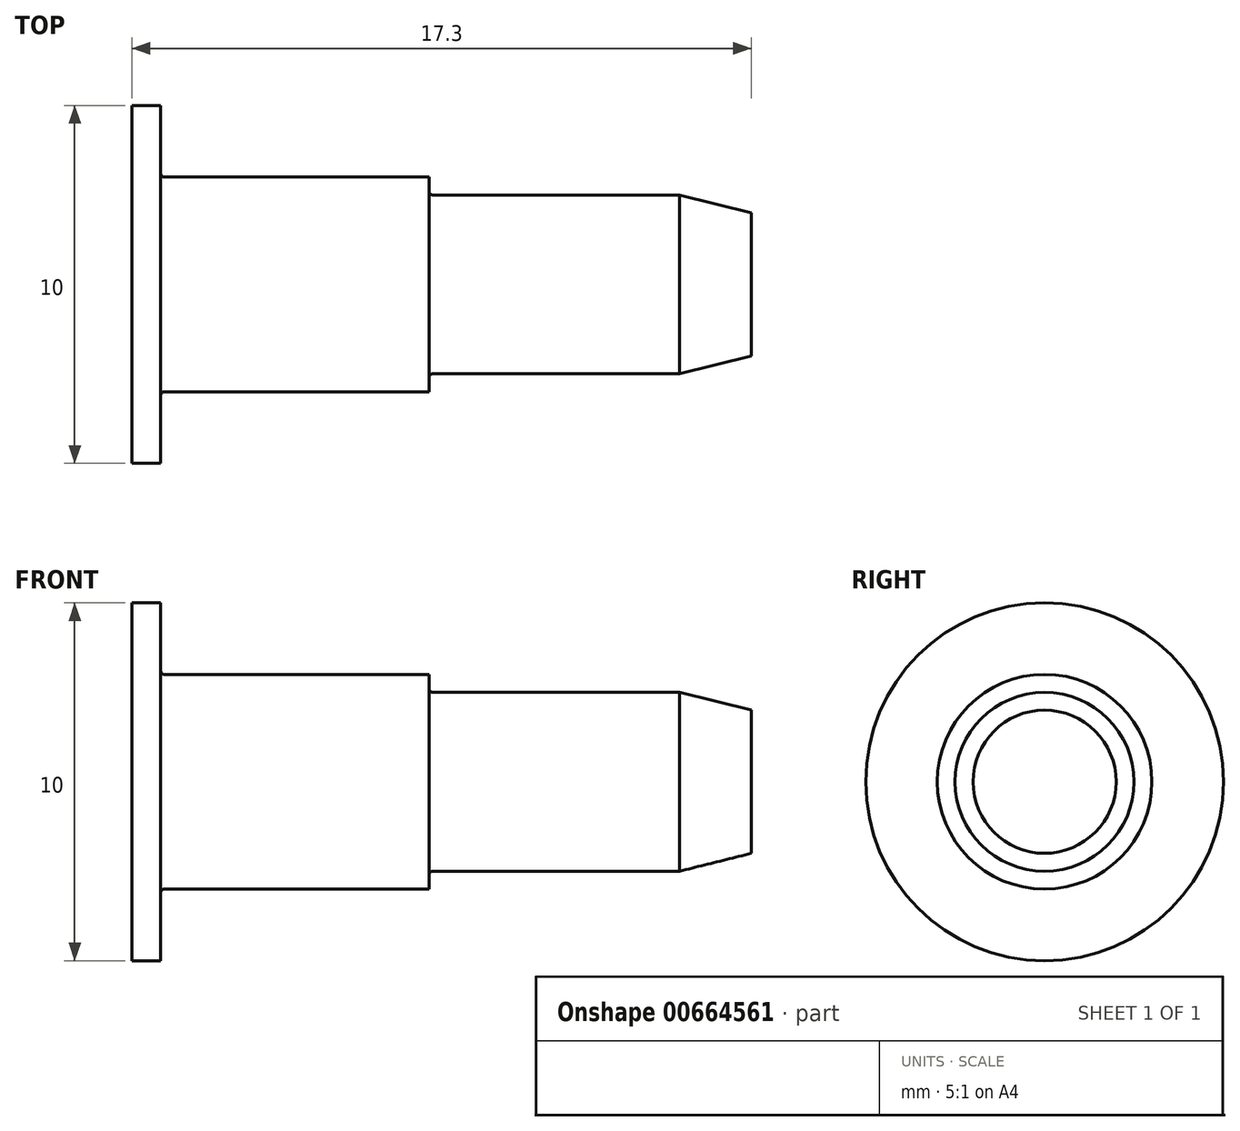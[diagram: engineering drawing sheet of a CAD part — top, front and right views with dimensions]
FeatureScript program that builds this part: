
annotation { "Feature Type Name" : "Feature", "Feature Type Description" : "" }
export const myFeature = defineFeature(function(context is Context, id is Id, definition is map)
    precondition{}
    {
        {
            var Q0;
            Q0=qCreatedBy(makeId("Front.planeOp"),FACE);
            var sketch = newSketch(context, id + "F0", { "sketchPlane" : qUnion([Q0])});
            skLineSegment(sketch, "E0", {"start": v(0, 0) * mm, "end": v(0, 5) * mm});
            skLineSegment(sketch, "E1", {"start": v(0, 5) * mm, "end": v(0.8, 5) * mm});
            skLineSegment(sketch, "E2", {"start": v(0.8, 5) * mm, "end": v(0.8, 3.1) * mm});
            skArc(sketch, "E3", {"start": v(0.8, 3.1) * mm, "mid": v(0.83, 3.03) * mm, "end": v(0.9, 3) * mm});
            skLineSegment(sketch, "E4", {"start": v(0.9, 3) * mm, "end": v(8.3, 3) * mm});
            skLineSegment(sketch, "E5", {"start": v(8.3, 3) * mm, "end": v(8.3, 2.6) * mm});
            skLineSegment(sketch, "E6", {"start": v(17.3, 2) * mm, "end": v(17.3, 0) * mm});
            skLineSegment(sketch, "E7", {"start": v(17.3, 0) * mm, "end": v(0, 0) * mm});
            skLineSegment(sketch, "E8", {"start": v(8.4, 2.5) * mm, "end": v(15.3, 2.5) * mm});
            skLineSegment(sketch, "E9", {"start": v(15.3, 2.5) * mm, "end": v(17.3, 2) * mm});
            skArc(sketch, "E10", {"start": v(8.3, 2.6) * mm, "mid": v(8.33, 2.53) * mm, "end": v(8.4, 2.5) * mm});
            skSolve(sketch);
        }
        {
            var Q0;
            Q0=makeQuery(id+"F0.imprint","IMPRINT",FACE,{"disambiguationData":[TD([[makeQuery(id+"F0.imprint","IMPRINT",EDGE,{"derivedFrom":sQuery(id+"F0.wireOp",EDGE,"E0")}),-1.0]])]});
            var Q1;
            Q1=sQuery(id+"F0.wireOp",EDGE,"E7");
            revolve(context, id + "F1", {"entities" : qUnion([Q0]), "axis" : qUnion([Q1]), "revolveType" : RevolveType.FULL});
        }
    });
